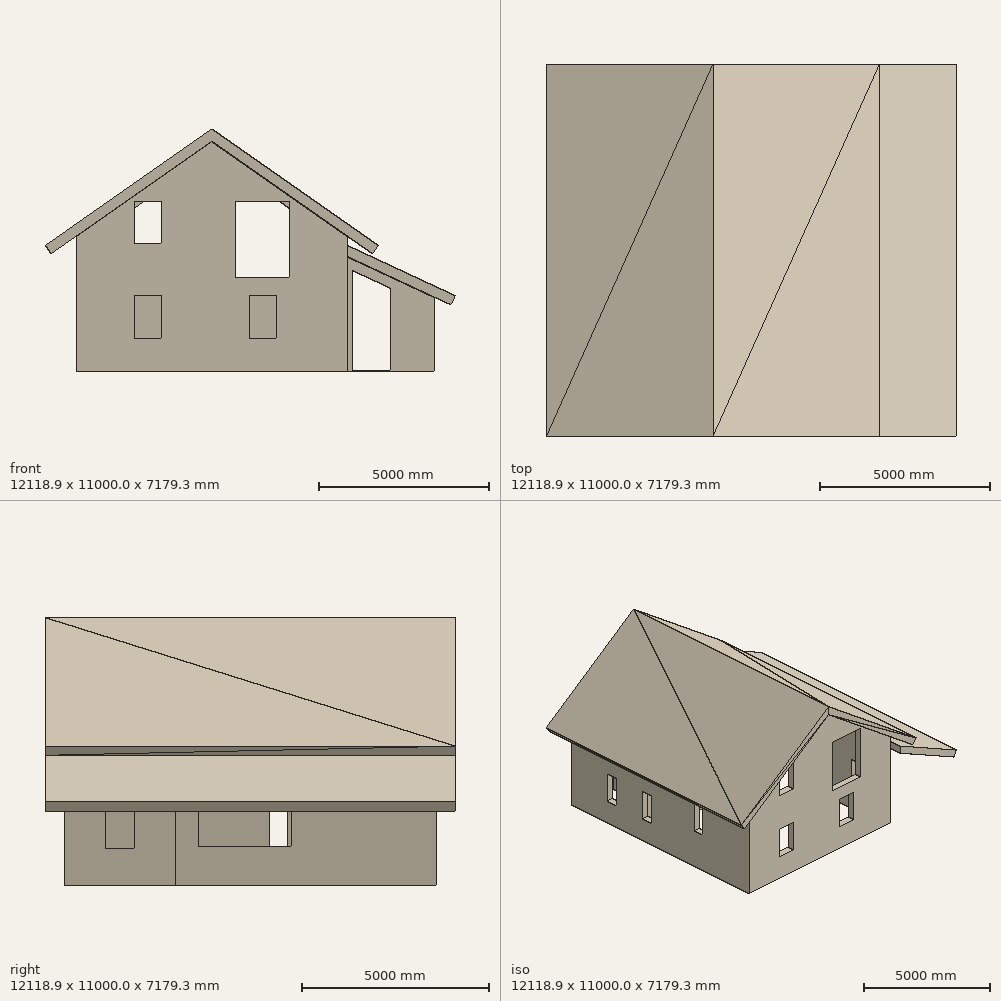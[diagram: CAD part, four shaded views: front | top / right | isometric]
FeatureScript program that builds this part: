
annotation { "Feature Type Name" : "Feature", "Feature Type Description" : "" }
export const myFeature = defineFeature(function(context is Context, id is Id, definition is map)
    precondition{}
    {
        {
            var Q0;
            Q0=qCreatedBy(makeId("Front.planeOp"),FACE);
            var sketch = newSketch(context, id + "F0", { "sketchPlane" : qUnion([Q0])});
            skLineSegment(sketch, "E0.bottom", {"start": v(0, 0) * mm, "end": v(8000, 0) * mm});
            skLineSegment(sketch, "E0.left", {"start": v(0, 0) * mm, "end": v(0, 4000) * mm});
            skLineSegment(sketch, "E0.right", {"start": v(8000, 0) * mm, "end": v(8000, 4000) * mm});
            skLineSegment(sketch, "E1", {"start": v(0, 4000) * mm, "end": v(4000, 6800.83) * mm});
            skPoint(sketch, "E1.endSnap0", {"position": v(4000, 5216.02) * mm});
            skLineSegment(sketch, "E2", {"start": v(4000, 6800.83) * mm, "end": v(8000, 4000) * mm});
            skSolve(sketch);
        }
        {
            var Q0;
            Q0=qSketchRegion(id+"F0",true);
            extrude(context, id + "F1", {"entities" : qUnion([Q0]), "depth" : 5000 * mm, "offsetDistance" : 25 * mm, "hasSecondDirection" : true, "secondDirectionOppositeDirection" : true, "secondDirectionDepth" : 5000 * mm});
        }
        {
            var Q0;
            Q0=qCreatedBy(makeId("Front.planeOp"),FACE);
            var sketch = newSketch(context, id + "F2", { "sketchPlane" : qUnion([Q0])});
            skLineSegment(sketch, "E3", {"start": v(4000, 6813.04) * mm, "end": v(-750, 3487.05) * mm});
            skLineSegment(sketch, "E4", {"start": v(-750, 3487.05) * mm, "end": v(-922.07, 3732.8) * mm});
            skLineSegment(sketch, "E5", {"start": v(-922.07, 3732.8) * mm, "end": v(4000, 7179.27) * mm});
            skLineSegment(sketch, "E6", {"start": v(4000, 7179.27) * mm, "end": v(8922.07, 3732.8) * mm});
            skLineSegment(sketch, "E7", {"start": v(8922.07, 3732.8) * mm, "end": v(8750, 3487.05) * mm});
            skLineSegment(sketch, "E8", {"start": v(8750, 3487.05) * mm, "end": v(4000, 6813.04) * mm});
            skLineSegment(sketch, "E9.0", {"start": v(0, 4000) * mm, "end": v(4000, 6800.83) * mm});
            skLineSegment(sketch, "E10.0", {"start": v(4000, 6800.83) * mm, "end": v(8000, 4000) * mm});
            skSolve(sketch);
        }
        {
            var Q0;
            Q0=makeQuery(id+"F2.imprint","IMPRINT",FACE,{"disambiguationData":[TD([[makeQuery(id+"F2.imprint","IMPRINT",EDGE,{"derivedFrom":sQuery(id+"F2.wireOp",EDGE,"E3")}),-1.0]])]});
            extrude(context, id + "F3", {"entities" : qUnion([Q0]), "depth" : 5500 * mm, "offsetDistance" : 25 * mm, "hasSecondDirection" : true, "secondDirectionOppositeDirection" : true, "secondDirectionDepth" : 5500 * mm});
        }
        {
            var Q0;
            Q0=qCreatedBy(makeId("Front.planeOp"),FACE);
            var sketch = newSketch(context, id + "F4", { "sketchPlane" : qUnion([Q0])});
            skPoint(sketch, "E11.0", {"position": v(8000, 0) * mm});
            skLineSegment(sketch, "E12", {"start": v(8000, 0) * mm, "end": v(10570, 0) * mm});
            skLineSegment(sketch, "E13", {"start": v(10570, 0) * mm, "end": v(10570, 2200) * mm});
            skLineSegment(sketch, "E14", {"start": v(10570, 2200) * mm, "end": v(8000, 3398.41) * mm});
            skLineSegment(sketch, "E15", {"start": v(8000, 3398.41) * mm, "end": v(8000, 0) * mm});
            skLineSegment(sketch, "E16.0", {"start": v(4000, 6800.83) * mm, "end": v(8000, 4000) * mm});
            skSolve(sketch);
        }
        {
            var Q0;
            Q0=makeQuery(id+"F4.imprint","IMPRINT",FACE,{"disambiguationData":[TD([[makeQuery(id+"F4.imprint","IMPRINT",EDGE,{"derivedFrom":sQuery(id+"F4.wireOp",EDGE,"E12")}),1.0]])]});
            extrude(context, id + "F5", {"entities" : qUnion([Q0]), "operationType" : NewBodyOperationType.ADD, "depth" : 2000 * mm, "offsetDistance" : 25 * mm, "hasSecondDirection" : true, "secondDirectionOppositeDirection" : true, "secondDirectionDepth" : 5000 * mm});
        }
        {
            var Q0;
            Q0=qCreatedBy(makeId("Front.planeOp"),FACE);
            var sketch = newSketch(context, id + "F6", { "sketchPlane" : qUnion([Q0])});
            skLineSegment(sketch, "E17.0", {"start": v(10570, 2200) * mm, "end": v(8000, 3398.41) * mm});
            skLineSegment(sketch, "E18", {"start": v(8010, 3735.8) * mm, "end": v(8010, 3404.78) * mm});
            skLineSegment(sketch, "E19", {"start": v(8010, 3404.78) * mm, "end": v(11070, 1977.88) * mm});
            skLineSegment(sketch, "E20", {"start": v(11070, 1977.88) * mm, "end": v(11196.79, 2249.77) * mm});
            skLineSegment(sketch, "E21", {"start": v(11196.79, 2249.77) * mm, "end": v(8010, 3735.8) * mm});
            skLineSegment(sketch, "E22.0.1", {"start": v(8000, 3398.41) * mm, "end": v(8000, 0) * mm});
            skLineSegment(sketch, "E22.0.2", {"start": v(8000, 0) * mm, "end": v(10570, 0) * mm});
            skLineSegment(sketch, "E22.0.3", {"start": v(10570, 0) * mm, "end": v(10570, 2200) * mm});
            skSolve(sketch);
        }
        {
            var Q0;
            Q0=makeQuery(id+"F6.imprint","IMPRINT",FACE,{"disambiguationData":[TD([[makeQuery(id+"F6.imprint","IMPRINT",EDGE,{"derivedFrom":sQuery(id+"F6.wireOp",EDGE,"E18")}),1.0]])]});
            extrude(context, id + "F7", {"entities" : qUnion([Q0]), "operationType" : NewBodyOperationType.ADD, "depth" : 5500 * mm, "offsetDistance" : 25 * mm, "hasSecondDirection" : true, "secondDirectionOppositeDirection" : true, "secondDirectionDepth" : 5500 * mm});
        }
        {
            var Q0;
            Q0=qCreatedBy(makeId("Front.planeOp"),FACE);
            var sketch = newSketch(context, id + "F8", { "sketchPlane" : qUnion([Q0])});
            skLineSegment(sketch, "E23.0.0", {"start": v(8000, 4000) * mm, "end": v(4000, 6800.83) * mm, "construction": true});
            skLineSegment(sketch, "E23.0.1", {"start": v(4000, 6800.83) * mm, "end": v(0, 4000) * mm, "construction": true});
            skLineSegment(sketch, "E23.0.2", {"start": v(0, 4000) * mm, "end": v(0, 0) * mm, "construction": true});
            skLineSegment(sketch, "E23.0.3", {"start": v(0, 0) * mm, "end": v(8000, 0) * mm, "construction": true});
            skLineSegment(sketch, "E23.0.4", {"start": v(8000, 0) * mm, "end": v(8000, 4000) * mm, "construction": true});
            skLineSegment(sketch, "E24", {"start": v(0, 2800) * mm, "end": v(8000, 2800) * mm});
            skSolve(sketch);
        }
        {
            var Q0;
            Q0=sQuery(id+"F8.wireOp",EDGE,"E24");
            cPlane(context, id + "F9", {"entities" : qUnion([Q0]), "cplaneType" : CPlaneType.LINE_ANGLE, "offset" : 25 * mm, "angle" : 90 * degree, "width" : 150 * mm, "height" : 150 * mm});
        }
        {
            var Q0;
            Q0=makeQuery(id+"F5.boolean.opBoolean","MERGE",FACE,{"derivedFrom":[makeQuery(id+"F1.opExtrude","SWEPT_FACE",FACE,{"disambiguationData":[OSD([sQuery(id+"F0.wireOp",EDGE,"E0.bottom")])]}),makeQuery(id+"F5.opExtrude","SWEPT_FACE",FACE,{"disambiguationData":[OSD([sQuery(id+"F4.wireOp",EDGE,"E12")])]})]});
            shell(context, id + "F10", {"entities" : qUnion([Q0]), "thickness" : 300 * mm});
        }
        {
            var Q0;
            Q0=makeQuery(id+"F5.opExtrude","CAP_FACE",FACE,{"disambiguationData":[OSD([sQuery(id+"F4.wireOp",EDGE,"E12"),sQuery(id+"F4.wireOp",EDGE,"E13"),sQuery(id+"F4.wireOp",EDGE,"E14"),sQuery(id+"F4.wireOp",EDGE,"E15")])],"isStart":false});
            var sketch = newSketch(context, id + "F11", { "sketchPlane" : qUnion([Q0])});
            skLineSegment(sketch, "E25.0.0", {"start": v(10570, 2200) * mm, "end": v(8000, 3398.41) * mm, "construction": true});
            skLineSegment(sketch, "E25.0.1", {"start": v(8000, 3398.41) * mm, "end": v(8000, 0) * mm, "construction": true});
            skLineSegment(sketch, "E25.0.2", {"start": v(8000, 0) * mm, "end": v(10570, 0) * mm, "construction": true});
            skLineSegment(sketch, "E25.0.3", {"start": v(10570, 0) * mm, "end": v(10570, 2200) * mm, "construction": true});
            skLineSegment(sketch, "E26", {"start": v(9285, 0) * mm, "end": v(9285, 2799.2) * mm});
            skLineSegment(sketch, "E27", {"start": v(9285, 2468.2) * mm, "end": v(8150, 2997.45) * mm});
            skLineSegment(sketch, "E28", {"start": v(8150, 2997.45) * mm, "end": v(8150, 50) * mm});
            skLineSegment(sketch, "E29", {"start": v(8150, 50) * mm, "end": v(9285, 50) * mm});
            skSolve(sketch);
        }
        {
            var Q0;
            {var subQ0=sQuery(id+"F11.wireOp",EDGE,"E27");Q0=makeQuery(id+"F11.imprint","IMPRINT",FACE,{"disambiguationData":[TD([[makeQuery(id+"F11.imprint","IMPRINT",EDGE,{"derivedFrom":subQ0}),1.0]])]});}
            extrude(context, id + "F12", {"entities" : qUnion([Q0]), "operationType" : NewBodyOperationType.REMOVE, "endBound" : BoundingType.THROUGH_ALL, "oppositeDirection" : true, "depth" : 25 * mm, "offsetDistance" : 25 * mm});
        }
        {
            var Q0;
            Q0=makeQuery(id+"F5.opExtrude","SWEPT_FACE",FACE,{"disambiguationData":[OSD([sQuery(id+"F4.wireOp",EDGE,"E13")])]});
            var sketch = newSketch(context, id + "F13", { "sketchPlane" : qUnion([Q0])});
            skLineSegment(sketch, "E30.bottom", {"start": v(-1400, 2050) * mm, "end": v(1100, 2050) * mm});
            skLineSegment(sketch, "E30.top", {"start": v(-1400, 1050) * mm, "end": v(1100, 1050) * mm});
            skLineSegment(sketch, "E30.left", {"start": v(-1400, 2050) * mm, "end": v(-1400, 1050) * mm});
            skLineSegment(sketch, "E30.right", {"start": v(1100, 2050) * mm, "end": v(1100, 1050) * mm});
            skSolve(sketch);
        }
        {
            var Q0;
            Q0=qSketchRegion(id+"F13",true);
            var Q1;
            Q1=makeQuery(id+"F13.imprint","IMPRINT",FACE,{"disambiguationData":[TD([[makeQuery(id+"F13.imprint","IMPRINT",EDGE,{"derivedFrom":sQuery(id+"F13.wireOp",EDGE,"E30.bottom")}),-1.0]])]});
            extrude(context, id + "F14", {"entities" : qUnion([Q0, Q1]), "operationType" : NewBodyOperationType.REMOVE, "endBound" : BoundingType.UP_TO_NEXT, "oppositeDirection" : true, "depth" : 25 * mm, "offsetDistance" : 25 * mm});
        }
        {
            var Q0;
            Q0=qCreatedBy(makeId("Top.planeOp"),FACE);
            var sketch = newSketch(context, id + "F15", { "sketchPlane" : qUnion([Q0])});
            skLineSegment(sketch, "E31.0", {"start": v(300, 4700) * mm, "end": v(10270, 4700) * mm});
            skLineSegment(sketch, "E32", {"start": v(6170, 4700) * mm, "end": v(6170, 1200) * mm});
            skLineSegment(sketch, "E33", {"start": v(6170, 1200) * mm, "end": v(2170, 1200) * mm});
            skLineSegment(sketch, "E34", {"start": v(2170, 1200) * mm, "end": v(2170, 4700) * mm});
            skLineSegment(sketch, "E35", {"start": v(2170, 4700) * mm, "end": v(2070, 4700) * mm});
            skLineSegment(sketch, "E36", {"start": v(2070, 4700) * mm, "end": v(2070, 1200) * mm});
            skLineSegment(sketch, "E37", {"start": v(300, 1100) * mm, "end": v(6270, 1100) * mm});
            skLineSegment(sketch, "E38", {"start": v(6270, 1100) * mm, "end": v(6270, 4700) * mm});
            skLineSegment(sketch, "E39.0", {"start": v(8000, -5000) * mm, "end": v(8000, -2000) * mm});
            skLineSegment(sketch, "E40.0", {"start": v(10270, -1700) * mm, "end": v(10270, 4700) * mm});
            skLineSegment(sketch, "E41", {"start": v(2070, 1200) * mm, "end": v(300, 1200) * mm});
            skLineSegment(sketch, "E42.0", {"start": v(300, -4700) * mm, "end": v(300, 4700) * mm});
            skSolve(sketch);
        }
        {
            var Q0;
            {var subQ0=sQuery(id+"F15.wireOp",EDGE,"E32");Q0=makeQuery(id+"F15.imprint","IMPRINT",FACE,{"disambiguationData":[TD([[makeQuery(id+"F15.imprint","IMPRINT",EDGE,{"derivedFrom":subQ0}),1.0]])]});}
            var Q1;
            Q1=qCreatedBy(id+"F9.planeOp",FACE);
            extrude(context, id + "F16", {"entities" : qUnion([Q0]), "operationType" : NewBodyOperationType.ADD, "endBound" : BoundingType.UP_TO_SURFACE, "depth" : 25 * mm, "endBoundEntityFace" : qUnion([Q1]), "offsetDistance" : 25 * mm});
        }
        {
            var Q0;
            Q0=makeQuery(id+"F1.opExtrude","SWEPT_FACE",FACE,{"disambiguationData":[OSD([sQuery(id+"F0.wireOp",EDGE,"E0.right")])]});
            var sketch = newSketch(context, id + "F17", { "sketchPlane" : qUnion([Q0])});
            skLineSegment(sketch, "E43.bottom", {"start": v(-3900, 2250) * mm, "end": v(-3100, 2250) * mm});
            skLineSegment(sketch, "E43.top", {"start": v(-3900, 1000) * mm, "end": v(-3100, 1000) * mm});
            skLineSegment(sketch, "E43.left", {"start": v(-3900, 2250) * mm, "end": v(-3900, 1000) * mm});
            skLineSegment(sketch, "E43.right", {"start": v(-3100, 2250) * mm, "end": v(-3100, 1000) * mm});
            skSolve(sketch);
        }
        {
            var Q0;
            Q0=makeQuery(id+"F17.imprint","IMPRINT",FACE,{"disambiguationData":[TD([[makeQuery(id+"F17.imprint","IMPRINT",EDGE,{"derivedFrom":sQuery(id+"F17.wireOp",EDGE,"E43.bottom")}),-1.0]])]});
            extrude(context, id + "F18", {"entities" : qUnion([Q0]), "operationType" : NewBodyOperationType.REMOVE, "endBound" : BoundingType.UP_TO_NEXT, "oppositeDirection" : true, "depth" : 25 * mm, "offsetDistance" : 25 * mm});
        }
        {
            var Q0;
            Q0=makeQuery(id+"F1.opExtrude","CAP_FACE",FACE,{"disambiguationData":[OSD([sQuery(id+"F0.wireOp",EDGE,"E0.bottom"),sQuery(id+"F0.wireOp",EDGE,"E0.left"),sQuery(id+"F0.wireOp",EDGE,"E0.right"),sQuery(id+"F0.wireOp",EDGE,"E1"),sQuery(id+"F0.wireOp",EDGE,"E2")])],"isStart":false});
            var sketch = newSketch(context, id + "F19", { "sketchPlane" : qUnion([Q0])});
            skLineSegment(sketch, "E44.bottom", {"start": v(1700, 2250) * mm, "end": v(2500, 2250) * mm});
            skLineSegment(sketch, "E44.top", {"start": v(1700, 1000) * mm, "end": v(2500, 1000) * mm});
            skLineSegment(sketch, "E44.left", {"start": v(1700, 2250) * mm, "end": v(1700, 1000) * mm});
            skLineSegment(sketch, "E44.right", {"start": v(2500, 2250) * mm, "end": v(2500, 1000) * mm});
            skLineSegment(sketch, "E45.bottom", {"start": v(5100, 2250) * mm, "end": v(5900, 2250) * mm});
            skLineSegment(sketch, "E45.top", {"start": v(5100, 1000) * mm, "end": v(5900, 1000) * mm});
            skLineSegment(sketch, "E45.left", {"start": v(5100, 2250) * mm, "end": v(5100, 1000) * mm});
            skLineSegment(sketch, "E45.right", {"start": v(5900, 2250) * mm, "end": v(5900, 1000) * mm});
            skLineSegment(sketch, "E46.bottom", {"start": v(1700, 3800) * mm, "end": v(2500, 3800) * mm});
            skLineSegment(sketch, "E46.top", {"start": v(1700, 5050) * mm, "end": v(2500, 5050) * mm});
            skLineSegment(sketch, "E46.left", {"start": v(1700, 3800) * mm, "end": v(1700, 5050) * mm});
            skLineSegment(sketch, "E46.right", {"start": v(2500, 3800) * mm, "end": v(2500, 5050) * mm});
            skLineSegment(sketch, "E47.bottom", {"start": v(4700, 5050) * mm, "end": v(6300, 5050) * mm});
            skLineSegment(sketch, "E47.top", {"start": v(4700, 2800) * mm, "end": v(6300, 2800) * mm});
            skLineSegment(sketch, "E47.left", {"start": v(4700, 5050) * mm, "end": v(4700, 2800) * mm});
            skLineSegment(sketch, "E47.right", {"start": v(6300, 5050) * mm, "end": v(6300, 2800) * mm});
            skSolve(sketch);
        }
        {
            var Q0;
            Q0=makeQuery(id+"F19.imprint","IMPRINT",FACE,{"disambiguationData":[TD([[makeQuery(id+"F19.imprint","IMPRINT",EDGE,{"derivedFrom":sQuery(id+"F19.wireOp",EDGE,"E46.bottom")}),1.0]])]});
            var Q1;
            Q1=makeQuery(id+"F19.imprint","IMPRINT",FACE,{"disambiguationData":[TD([[makeQuery(id+"F19.imprint","IMPRINT",EDGE,{"derivedFrom":sQuery(id+"F19.wireOp",EDGE,"E47.bottom")}),-1.0]])]});
            var Q2;
            Q2=makeQuery(id+"F19.imprint","IMPRINT",FACE,{"disambiguationData":[TD([[makeQuery(id+"F19.imprint","IMPRINT",EDGE,{"derivedFrom":sQuery(id+"F19.wireOp",EDGE,"E45.bottom")}),-1.0]])]});
            var Q3;
            Q3=makeQuery(id+"F19.imprint","IMPRINT",FACE,{"disambiguationData":[TD([[makeQuery(id+"F19.imprint","IMPRINT",EDGE,{"derivedFrom":sQuery(id+"F19.wireOp",EDGE,"E44.bottom")}),-1.0]])]});
            extrude(context, id + "F20", {"entities" : qUnion([Q0, Q1, Q2, Q3]), "operationType" : NewBodyOperationType.REMOVE, "oppositeDirection" : true, "depth" : 300 * mm, "offsetDistance" : 25 * mm});
        }
        {
            var Q0;
            Q0=makeQuery(id+"F5.boolean.opBoolean","MERGE",FACE,{"derivedFrom":[makeQuery(id+"F1.opExtrude","CAP_FACE",FACE,{"disambiguationData":[OSD([sQuery(id+"F0.wireOp",EDGE,"E0.bottom"),sQuery(id+"F0.wireOp",EDGE,"E0.left"),sQuery(id+"F0.wireOp",EDGE,"E0.right"),sQuery(id+"F0.wireOp",EDGE,"E1"),sQuery(id+"F0.wireOp",EDGE,"E2")])],"isStart":true}),makeQuery(id+"F5.opExtrude","CAP_FACE",FACE,{"disambiguationData":[OSD([sQuery(id+"F4.wireOp",EDGE,"E12"),sQuery(id+"F4.wireOp",EDGE,"E13"),sQuery(id+"F4.wireOp",EDGE,"E14"),sQuery(id+"F4.wireOp",EDGE,"E15")])],"isStart":true})]});
            var sketch = newSketch(context, id + "F21", { "sketchPlane" : qUnion([Q0])});
            skLineSegment(sketch, "E48.0", {"start": v(-1700, 5050) * mm, "end": v(-2500, 5050) * mm});
            skLineSegment(sketch, "E49.0", {"start": v(-2500, 3800) * mm, "end": v(-2500, 5050) * mm});
            skLineSegment(sketch, "E50.0", {"start": v(-1700, 3800) * mm, "end": v(-1700, 5050) * mm});
            skLineSegment(sketch, "E51.0", {"start": v(-1700, 3800) * mm, "end": v(-2500, 3800) * mm});
            skLineSegment(sketch, "E52.0", {"start": v(-4700, 5050) * mm, "end": v(-6300, 5050) * mm});
            skLineSegment(sketch, "E53.0", {"start": v(-4700, 5050) * mm, "end": v(-4700, 2800) * mm});
            skLineSegment(sketch, "E54.0", {"start": v(-6300, 5050) * mm, "end": v(-6300, 2800) * mm});
            skLineSegment(sketch, "E55.0", {"start": v(-4700, 2800) * mm, "end": v(-6300, 2800) * mm});
            skLineSegment(sketch, "E56.0", {"start": v(-1700, 2250) * mm, "end": v(-2500, 2250) * mm});
            skLineSegment(sketch, "E57.0", {"start": v(-1700, 2250) * mm, "end": v(-1700, 1000) * mm});
            skLineSegment(sketch, "E58.0", {"start": v(-1700, 1000) * mm, "end": v(-2500, 1000) * mm});
            skLineSegment(sketch, "E59.0", {"start": v(-2500, 2250) * mm, "end": v(-2500, 1000) * mm});
            skLineSegment(sketch, "E60.bottom", {"start": v(-6300, 2250) * mm, "end": v(-4700, 2250) * mm});
            skLineSegment(sketch, "E60.top", {"start": v(-6300, 1000) * mm, "end": v(-4700, 1000) * mm});
            skLineSegment(sketch, "E60.left", {"start": v(-6300, 2250) * mm, "end": v(-6300, 1000) * mm});
            skLineSegment(sketch, "E60.right", {"start": v(-4700, 2250) * mm, "end": v(-4700, 1000) * mm});
            skSolve(sketch);
        }
        {
            var Q0;
            Q0=makeQuery(id+"F21.imprint","IMPRINT",FACE,{"disambiguationData":[TD([[makeQuery(id+"F21.imprint","IMPRINT",EDGE,{"derivedFrom":sQuery(id+"F21.wireOp",EDGE,"E52.0")}),1.0]])]});
            var Q1;
            Q1=makeQuery(id+"F21.imprint","IMPRINT",FACE,{"disambiguationData":[TD([[makeQuery(id+"F21.imprint","IMPRINT",EDGE,{"derivedFrom":sQuery(id+"F21.wireOp",EDGE,"E48.0")}),1.0]])]});
            var Q2;
            Q2=makeQuery(id+"F21.imprint","IMPRINT",FACE,{"disambiguationData":[TD([[makeQuery(id+"F21.imprint","IMPRINT",EDGE,{"derivedFrom":sQuery(id+"F21.wireOp",EDGE,"E56.0")}),1.0]])]});
            var Q3;
            Q3=makeQuery(id+"F21.imprint","IMPRINT",FACE,{"disambiguationData":[TD([[makeQuery(id+"F21.imprint","IMPRINT",EDGE,{"derivedFrom":sQuery(id+"F21.wireOp",EDGE,"E60.bottom")}),-1.0]])]});
            var Q4;
            Q4=makeQuery(id+"F10.opShell","OFFSET_FACE",FACE,{"disambiguationData":[OSD([sQuery(id+"F0.wireOp",EDGE,"E0.bottom"),sQuery(id+"F0.wireOp",EDGE,"E0.left"),sQuery(id+"F0.wireOp",EDGE,"E0.right"),sQuery(id+"F0.wireOp",EDGE,"E1"),sQuery(id+"F0.wireOp",EDGE,"E2"),sQuery(id+"F4.wireOp",EDGE,"E12"),sQuery(id+"F4.wireOp",EDGE,"E13"),sQuery(id+"F4.wireOp",EDGE,"E14"),sQuery(id+"F4.wireOp",EDGE,"E15")])]});
            extrude(context, id + "F22", {"entities" : qUnion([Q0, Q1, Q2, Q3, Q4]), "operationType" : NewBodyOperationType.REMOVE, "oppositeDirection" : true, "depth" : 300 * mm, "offsetDistance" : 25 * mm});
        }
        {
            var Q0;
            Q0=makeQuery(id+"F1.opExtrude","SWEPT_FACE",FACE,{"disambiguationData":[OSD([sQuery(id+"F0.wireOp",EDGE,"E0.left")])]});
            var sketch = newSketch(context, id + "F23", { "sketchPlane" : qUnion([Q0])});
            skLineSegment(sketch, "E61.0", {"start": v(5000, 0) * mm, "end": v(-5000, 0) * mm});
            skLineSegment(sketch, "E62.bottom", {"start": v(1200, 0) * mm, "end": v(200, 0) * mm});
            skLineSegment(sketch, "E62.top", {"start": v(1200, 2250) * mm, "end": v(200, 2250) * mm});
            skLineSegment(sketch, "E62.left", {"start": v(1200, 0) * mm, "end": v(1200, 2250) * mm});
            skLineSegment(sketch, "E62.right", {"start": v(200, 0) * mm, "end": v(200, 2250) * mm});
            skLineSegment(sketch, "E63.bottom", {"start": v(-500, 2250) * mm, "end": v(-1000, 2250) * mm});
            skLineSegment(sketch, "E63.top", {"start": v(-500, 1000) * mm, "end": v(-1000, 1000) * mm});
            skLineSegment(sketch, "E63.left", {"start": v(-500, 2250) * mm, "end": v(-500, 1000) * mm});
            skLineSegment(sketch, "E63.right", {"start": v(-1000, 2250) * mm, "end": v(-1000, 1000) * mm});
            skLineSegment(sketch, "E64.bottom", {"start": v(-2500, 2250) * mm, "end": v(-3000, 2250) * mm});
            skLineSegment(sketch, "E64.top", {"start": v(-2500, 1000) * mm, "end": v(-3000, 1000) * mm});
            skLineSegment(sketch, "E64.left", {"start": v(-2500, 2250) * mm, "end": v(-2500, 1000) * mm});
            skLineSegment(sketch, "E64.right", {"start": v(-3000, 2250) * mm, "end": v(-3000, 1000) * mm});
            skLineSegment(sketch, "E65.bottom", {"start": v(1900, 3625) * mm, "end": v(2400, 3625) * mm});
            skLineSegment(sketch, "E65.top", {"start": v(1900, 1625) * mm, "end": v(2400, 1625) * mm});
            skLineSegment(sketch, "E65.left", {"start": v(1900, 3625) * mm, "end": v(1900, 1625) * mm});
            skLineSegment(sketch, "E65.right", {"start": v(2400, 3625) * mm, "end": v(2400, 1625) * mm});
            skSolve(sketch);
        }
        {
            var Q0;
            Q0=makeQuery(id+"F23.imprint","IMPRINT",FACE,{"disambiguationData":[TD([[makeQuery(id+"F23.imprint","IMPRINT",EDGE,{"derivedFrom":sQuery(id+"F23.wireOp",EDGE,"E64.bottom")}),1.0]])]});
            var Q1;
            Q1=makeQuery(id+"F23.imprint","IMPRINT",FACE,{"disambiguationData":[TD([[makeQuery(id+"F23.imprint","IMPRINT",EDGE,{"derivedFrom":sQuery(id+"F23.wireOp",EDGE,"E63.bottom")}),1.0]])]});
            var Q2;
            Q2=makeQuery(id+"F23.imprint","IMPRINT",FACE,{"disambiguationData":[TD([[makeQuery(id+"F23.imprint","IMPRINT",EDGE,{"derivedFrom":sQuery(id+"F23.wireOp",EDGE,"E62.bottom")}),-1.0]])]});
            var Q3;
            Q3=makeQuery(id+"F23.imprint","IMPRINT",FACE,{"disambiguationData":[TD([[makeQuery(id+"F23.imprint","IMPRINT",EDGE,{"derivedFrom":sQuery(id+"F23.wireOp",EDGE,"E65.bottom")}),-1.0]])]});
            extrude(context, id + "F24", {"entities" : qUnion([Q0, Q1, Q2, Q3]), "operationType" : NewBodyOperationType.REMOVE, "endBound" : BoundingType.UP_TO_NEXT, "oppositeDirection" : true, "depth" : 25 * mm, "offsetDistance" : 25 * mm});
        }
    });
